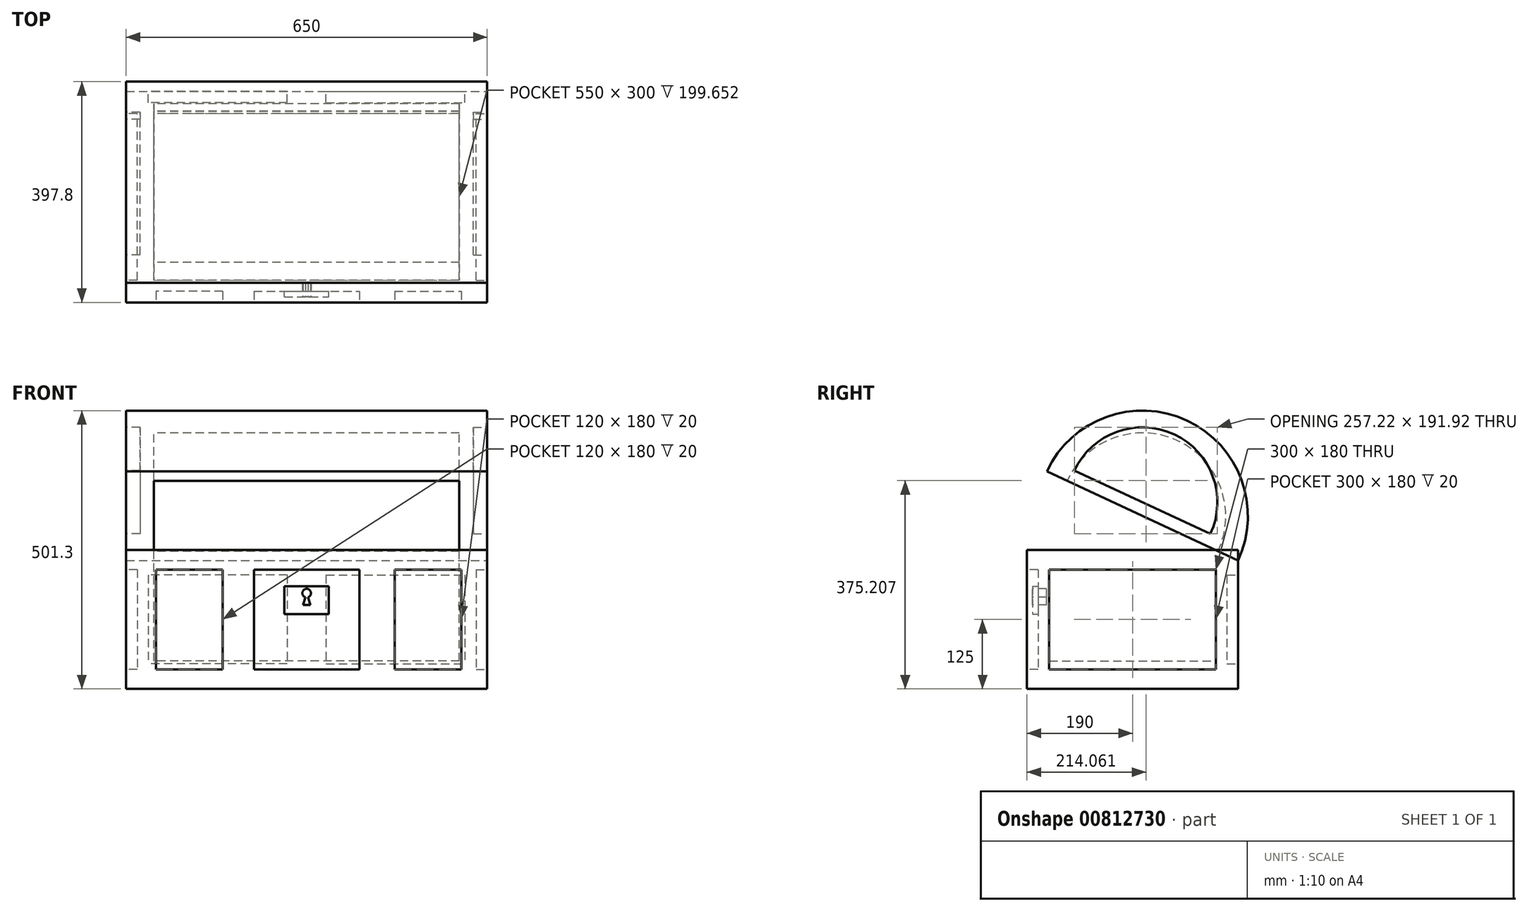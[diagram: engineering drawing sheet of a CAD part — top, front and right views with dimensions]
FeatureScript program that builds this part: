
annotation { "Feature Type Name" : "Feature", "Feature Type Description" : "" }
export const myFeature = defineFeature(function(context is Context, id is Id, definition is map)
    precondition{}
    {
        {
            var Q0;
            Q0=qCreatedBy(makeId("Top.planeOp"),FACE);
            var sketch = newSketch(context, id + "F0", { "sketchPlane" : qUnion([Q0])});
            skLineSegment(sketch, "E0.bottom", {"start": v(-32.5, 19) * mm, "end": v(32.5, 19) * mm});
            skLineSegment(sketch, "E0.top", {"start": v(-32.5, -19) * mm, "end": v(32.5, -19) * mm});
            skLineSegment(sketch, "E0.left", {"start": v(-32.5, 19) * mm, "end": v(-32.5, -19) * mm});
            skLineSegment(sketch, "E0.right", {"start": v(32.5, 19) * mm, "end": v(32.5, -19) * mm});
            skPoint(sketch, "E0.middle", {"position": v(0, 0) * mm});
            skSolve(sketch);
        }
        {
            var Q0;
            Q0 = qSketchRegion(id + "F0", true);
            extrude(context, id + "F1", {"entities" : qUnion([Q0]), "depth" : 25 * mm, "offsetDistance" : 25 * mm});
        }
        {
            var Q0;
            Q0=qCreatedBy(makeId("Right.planeOp"),FACE);
            var sketch = newSketch(context, id + "F2", { "sketchPlane" : qUnion([Q0])});
            skArc(sketch, "E1", {"start": v(-19, 23.1) * mm, "mid": v(-9.8, 48.35) * mm, "end": v(15.44, 39.16) * mm});
            skLineSegment(sketch, "E2", {"start": v(15.44, 39.16) * mm, "end": v(-19, 23.1) * mm});
            skSolve(sketch);
        }
        {
            var Q0;
            Q0 = qSketchRegion(id + "F2", true);
            extrude(context, id + "F3", {"entities" : qUnion([Q0]), "endBound" : BoundingType.SYMMETRIC, "depth" : 65 * mm, "offsetDistance" : 25 * mm});
        }
        {
            var Q0;
            Q0=qCreatedBy(makeId("Right.planeOp"),FACE);
            var sketch = newSketch(context, id + "F4", { "sketchPlane" : qUnion([Q0])});
            skArc(sketch, "E3", {"start": v(-15.37, 24.8) * mm, "mid": v(-8.12, 44.72) * mm, "end": v(11.81, 37.47) * mm});
            skLineSegment(sketch, "E4", {"start": v(11.81, 37.47) * mm, "end": v(-15.37, 24.8) * mm});
            skSolve(sketch);
        }
        {
            var Q0;
            Q0 = qSketchRegion(id + "F4", true);
            extrude(context, id + "F5", {"entities" : qUnion([Q0]), "operationType" : NewBodyOperationType.REMOVE, "endBound" : BoundingType.SYMMETRIC, "oppositeDirection" : true, "depth" : 55 * mm, "offsetDistance" : 25 * mm});
        }
        {
            var Q0;
            Q0=makeQuery(id+"F3.opExtrude","CAP_FACE",FACE,{"disambiguationData":[OSD([sQuery(id+"F2.wireOp",EDGE,"E1"),sQuery(id+"F2.wireOp",EDGE,"E2")])],"isStart":false});
            var sketch = newSketch(context, id + "F6", { "sketchPlane" : qUnion([Q0])});
            skArc(sketch, "E5", {"start": v(-14.02, 25.42) * mm, "mid": v(-7.49, 43.36) * mm, "end": v(10.46, 36.84) * mm});
            skLineSegment(sketch, "E6", {"start": v(-14.02, 25.42) * mm, "end": v(10.46, 36.84) * mm});
            skSolve(sketch);
        }
        {
            var Q0;
            Q0 = qSketchRegion(id + "F6", true);
            extrude(context, id + "F7", {"entities" : qUnion([Q0]), "oppositeDirection" : true, "depth" : 2.5 * mm, "offsetDistance" : 25 * mm});
        }
        {
            var Q0;
            Q0=makeQuery(id+"F7.opExtrude","SWEPT_BODY",BODY,{"disambiguationData":[OSD([sQuery(id+"F6.wireOp",EDGE,"E5"),sQuery(id+"F6.wireOp",EDGE,"E6")])]});
            transform(context, id + "F8", {"entities" : qUnion([Q0]), "transformType" : TransformType.TRANSLATION_3D, "dx" : 0 * mm, "dy" : 0 * mm, "dz" : 2.5 * mm, "makeCopy" : false});
        }
        {
            var Q0;
            Q0=makeQuery(id+"F7.opExtrude","SWEPT_BODY",BODY,{"disambiguationData":[OSD([sQuery(id+"F6.wireOp",EDGE,"E5"),sQuery(id+"F6.wireOp",EDGE,"E6")])]});
            var Q1;
            Q1=qCreatedBy(makeId("Right.planeOp"),FACE);
            mirror(context, id + "F9", {"entities" : qUnion([Q0]), "mirrorPlane" : qUnion([Q1])});
        }
        {
            var Q0;
            Q0=makeQuery(id+"F9.opPattern","COPY",BODY,{"derivedFrom":makeQuery(id+"F7.opExtrude","SWEPT_BODY",BODY,{"disambiguationData":[OSD([sQuery(id+"F6.wireOp",EDGE,"E5"),sQuery(id+"F6.wireOp",EDGE,"E6")])]}),"instanceName":"1"});
            var Q1;
            Q1=makeQuery(id+"F7.opExtrude","SWEPT_BODY",BODY,{"disambiguationData":[OSD([sQuery(id+"F6.wireOp",EDGE,"E5"),sQuery(id+"F6.wireOp",EDGE,"E6")])]});
            var Q2;
            Q2=makeQuery(id+"F3.opExtrude","SWEPT_BODY",BODY,{"disambiguationData":[OSD([sQuery(id+"F2.wireOp",EDGE,"E1"),sQuery(id+"F2.wireOp",EDGE,"E2")])]});
            booleanBodies(context, id + "F10", {"operationType" : BooleanOperationType.SUBTRACTION, "tools" : qUnion([Q0, Q1]), "targets" : qUnion([Q2])});
        }
        {
            var Q0;
            Q0=makeQuery(id+"F1.opExtrude","CAP_FACE",FACE,{"disambiguationData":[OSD([sQuery(id+"F0.wireOp",EDGE,"E0.bottom"),sQuery(id+"F0.wireOp",EDGE,"E0.top"),sQuery(id+"F0.wireOp",EDGE,"E0.left"),sQuery(id+"F0.wireOp",EDGE,"E0.right")])],"isStart":false});
            var sketch = newSketch(context, id + "F11", { "sketchPlane" : qUnion([Q0])});
            skLineSegment(sketch, "E7.bottom", {"start": v(-27.5, 15) * mm, "end": v(27.5, 15) * mm});
            skLineSegment(sketch, "E7.top", {"start": v(-27.5, -15) * mm, "end": v(27.5, -15) * mm});
            skLineSegment(sketch, "E7.left", {"start": v(-27.5, 15) * mm, "end": v(-27.5, -15) * mm});
            skLineSegment(sketch, "E7.right", {"start": v(27.5, 15) * mm, "end": v(27.5, -15) * mm});
            skPoint(sketch, "E7.middle", {"position": v(0, 0) * mm});
            skSolve(sketch);
        }
        {
            var Q0;
            Q0 = qSketchRegion(id + "F11", true);
            extrude(context, id + "F12", {"entities" : qUnion([Q0]), "operationType" : NewBodyOperationType.REMOVE, "oppositeDirection" : true, "depth" : 20 * mm, "offsetDistance" : 25 * mm});
        }
        {
            var Q0;
            Q0=makeQuery(id+"F1.opExtrude","SWEPT_FACE",FACE,{"disambiguationData":[OSD([sQuery(id+"F0.wireOp",EDGE,"E0.left")])]});
            var sketch = newSketch(context, id + "F13", { "sketchPlane" : qUnion([Q0])});
            skPoint(sketch, "E8", {"position": v(0, 12.5) * mm});
            skPoint(sketch, "E8.positionSnap0", {"position": v(-19, 12.5) * mm});
            skPoint(sketch, "E8.positionSnap1", {"position": v(0, 25) * mm});
            skLineSegment(sketch, "E9.bottom", {"start": v(-15, 21.5) * mm, "end": v(15, 21.5) * mm});
            skLineSegment(sketch, "E9.top", {"start": v(-15, 3.5) * mm, "end": v(15, 3.5) * mm});
            skLineSegment(sketch, "E9.left", {"start": v(-15, 21.5) * mm, "end": v(-15, 3.5) * mm});
            skLineSegment(sketch, "E9.right", {"start": v(15, 21.5) * mm, "end": v(15, 3.5) * mm});
            skSolve(sketch);
        }
        {
            var Q0;
            Q0 = qSketchRegion(id + "F13", true);
            extrude(context, id + "F14", {"entities" : qUnion([Q0]), "oppositeDirection" : true, "depth" : 2 * mm, "offsetDistance" : 25 * mm});
        }
        {
            var Q0;
            Q0=makeQuery(id+"F14.opExtrude","SWEPT_BODY",BODY,{"disambiguationData":[OSD([sQuery(id+"F13.wireOp",EDGE,"E9.bottom"),sQuery(id+"F13.wireOp",EDGE,"E9.top"),sQuery(id+"F13.wireOp",EDGE,"E9.left"),sQuery(id+"F13.wireOp",EDGE,"E9.right")])]});
            var Q1;
            Q1=qCreatedBy(makeId("Right.planeOp"),FACE);
            mirror(context, id + "F15", {"entities" : qUnion([Q0]), "mirrorPlane" : qUnion([Q1])});
        }
        {
            var Q0;
            Q0=makeQuery(id+"F15.opPattern","COPY",BODY,{"derivedFrom":makeQuery(id+"F14.opExtrude","SWEPT_BODY",BODY,{"disambiguationData":[OSD([sQuery(id+"F13.wireOp",EDGE,"E9.bottom"),sQuery(id+"F13.wireOp",EDGE,"E9.top"),sQuery(id+"F13.wireOp",EDGE,"E9.left"),sQuery(id+"F13.wireOp",EDGE,"E9.right")])]}),"instanceName":"1"});
            var Q1;
            Q1=makeQuery(id+"F14.opExtrude","SWEPT_BODY",BODY,{"disambiguationData":[OSD([sQuery(id+"F13.wireOp",EDGE,"E9.bottom"),sQuery(id+"F13.wireOp",EDGE,"E9.top"),sQuery(id+"F13.wireOp",EDGE,"E9.left"),sQuery(id+"F13.wireOp",EDGE,"E9.right")])]});
            var Q2;
            Q2=makeQuery(id+"F1.opExtrude","SWEPT_BODY",BODY,{"disambiguationData":[OSD([sQuery(id+"F0.wireOp",EDGE,"E0.bottom"),sQuery(id+"F0.wireOp",EDGE,"E0.top"),sQuery(id+"F0.wireOp",EDGE,"E0.left"),sQuery(id+"F0.wireOp",EDGE,"E0.right")])]});
            booleanBodies(context, id + "F16", {"operationType" : BooleanOperationType.SUBTRACTION, "tools" : qUnion([Q0, Q1]), "targets" : qUnion([Q2])});
        }
        {
            var Q0;
            Q0=makeQuery(id+"F1.opExtrude","SWEPT_FACE",FACE,{"disambiguationData":[OSD([sQuery(id+"F0.wireOp",EDGE,"E0.bottom")])]});
            var sketch = newSketch(context, id + "F17", { "sketchPlane" : qUnion([Q0])});
            skLineSegment(sketch, "E10.bottom", {"start": v(-9.5, 21.5) * mm, "end": v(9.5, 21.5) * mm});
            skLineSegment(sketch, "E10.top", {"start": v(-9.5, 3.5) * mm, "end": v(9.5, 3.5) * mm});
            skLineSegment(sketch, "E10.left", {"start": v(-9.5, 21.5) * mm, "end": v(-9.5, 3.5) * mm});
            skLineSegment(sketch, "E10.right", {"start": v(9.5, 21.5) * mm, "end": v(9.5, 3.5) * mm});
            skPoint(sketch, "E10.middle", {"position": v(0, 12.5) * mm});
            skPoint(sketch, "E10.middle.positionSnap0", {"position": v(-32.5, 12.5) * mm});
            skPoint(sketch, "E10.middle.positionSnap1", {"position": v(0, 25) * mm});
            skPoint(sketch, "E10.centerSnap0", {"position": v(-32.5, 12.5) * mm});
            skPoint(sketch, "E10.centerSnap1", {"position": v(0, 25) * mm});
            skLineSegment(sketch, "E11.bottom", {"start": v(-15.1, 21.5) * mm, "end": v(-27.1, 21.5) * mm});
            skLineSegment(sketch, "E11.top", {"start": v(-15.1, 3.5) * mm, "end": v(-27.1, 3.5) * mm});
            skLineSegment(sketch, "E11.left", {"start": v(-15.1, 21.5) * mm, "end": v(-15.1, 3.5) * mm});
            skLineSegment(sketch, "E11.right", {"start": v(-27.1, 21.5) * mm, "end": v(-27.1, 3.5) * mm});
            skPoint(sketch, "E11.middle", {"position": v(-21.1, 12.5) * mm});
            skLineSegment(sketch, "E12.bottom", {"start": v(15.85, 21.5) * mm, "end": v(27.85, 21.5) * mm});
            skLineSegment(sketch, "E12.top", {"start": v(15.85, 3.5) * mm, "end": v(27.85, 3.5) * mm});
            skLineSegment(sketch, "E12.left", {"start": v(15.85, 21.5) * mm, "end": v(15.85, 3.5) * mm});
            skLineSegment(sketch, "E12.right", {"start": v(27.85, 21.5) * mm, "end": v(27.85, 3.5) * mm});
            skPoint(sketch, "E12.middle", {"position": v(21.85, 12.5) * mm});
            skPoint(sketch, "E12.middle.positionSnap0", {"position": v(32.5, 12.5) * mm});
            skPoint(sketch, "E12.cornerSnap0", {"position": v(-21.1, 21.5) * mm});
            skPoint(sketch, "E12.centerSnap0", {"position": v(32.5, 12.5) * mm});
            skSolve(sketch);
        }
        {
            var Q0;
            Q0=makeQuery(id+"F17.imprint","IMPRINT",FACE,{"disambiguationData":[TD([[makeQuery(id+"F17.imprint","IMPRINT",EDGE,{"derivedFrom":sQuery(id+"F17.wireOp",EDGE,"E11.bottom")}),1.0]])]});
            var Q1;
            Q1=makeQuery(id+"F17.imprint","IMPRINT",FACE,{"disambiguationData":[TD([[makeQuery(id+"F17.imprint","IMPRINT",EDGE,{"derivedFrom":sQuery(id+"F17.wireOp",EDGE,"E10.bottom")}),-1.0]])]});
            var Q2;
            Q2=makeQuery(id+"F17.imprint","IMPRINT",FACE,{"disambiguationData":[TD([[makeQuery(id+"F17.imprint","IMPRINT",EDGE,{"derivedFrom":sQuery(id+"F17.wireOp",EDGE,"E12.bottom")}),-1.0]])]});
            extrude(context, id + "F18", {"entities" : qUnion([Q0, Q1, Q2]), "operationType" : NewBodyOperationType.REMOVE, "oppositeDirection" : true, "depth" : 2 * mm, "offsetDistance" : 25 * mm});
        }
        {
            var Q0;
            Q0=makeQuery(id+"F1.opExtrude","SWEPT_FACE",FACE,{"disambiguationData":[OSD([sQuery(id+"F0.wireOp",EDGE,"E0.top")])]});
            var sketch = newSketch(context, id + "F19", { "sketchPlane" : qUnion([Q0])});
            skLineSegment(sketch, "E13.bottom", {"start": v(-3.5, 20.5) * mm, "end": v(-28.5, 20.5) * mm});
            skLineSegment(sketch, "E13.top", {"start": v(-3.5, 4.5) * mm, "end": v(-28.5, 4.5) * mm});
            skLineSegment(sketch, "E13.left", {"start": v(-3.5, 20.5) * mm, "end": v(-3.5, 4.5) * mm});
            skLineSegment(sketch, "E13.right", {"start": v(-28.5, 20.5) * mm, "end": v(-28.5, 4.5) * mm});
            skPoint(sketch, "E13.middle", {"position": v(-16, 12.5) * mm});
            skPoint(sketch, "E13.middle.positionSnap0", {"position": v(-32.5, 12.5) * mm});
            skPoint(sketch, "E13.centerSnap0", {"position": v(-32.5, 12.5) * mm});
            skLineSegment(sketch, "E14.bottom", {"start": v(3.5, 20.5) * mm, "end": v(28.5, 20.5) * mm});
            skLineSegment(sketch, "E14.top", {"start": v(3.5, 4.5) * mm, "end": v(28.5, 4.5) * mm});
            skLineSegment(sketch, "E14.left", {"start": v(3.5, 20.5) * mm, "end": v(3.5, 4.5) * mm});
            skLineSegment(sketch, "E14.right", {"start": v(28.5, 20.5) * mm, "end": v(28.5, 4.5) * mm});
            skPoint(sketch, "E14.middle", {"position": v(16, 12.5) * mm});
            skSolve(sketch);
        }
        {
            var Q0;
            Q0=makeQuery(id+"F19.imprint","IMPRINT",FACE,{"disambiguationData":[TD([[makeQuery(id+"F19.imprint","IMPRINT",EDGE,{"derivedFrom":sQuery(id+"F19.wireOp",EDGE,"E13.bottom")}),1.0]])]});
            var Q1;
            Q1=makeQuery(id+"F19.imprint","IMPRINT",FACE,{"disambiguationData":[TD([[makeQuery(id+"F19.imprint","IMPRINT",EDGE,{"derivedFrom":sQuery(id+"F19.wireOp",EDGE,"E14.bottom")}),-1.0]])]});
            extrude(context, id + "F20", {"entities" : qUnion([Q0, Q1]), "operationType" : NewBodyOperationType.REMOVE, "oppositeDirection" : true, "depth" : 2 * mm, "offsetDistance" : 25 * mm});
        }
        {
            var Q0;
            Q0=makeQuery(id+"F18.boolean.opBoolean","COPY",FACE,{"derivedFrom":makeQuery(id+"F18.opExtrude","CAP_FACE",FACE,{"disambiguationData":[OSD([sQuery(id+"F17.wireOp",EDGE,"E10.bottom"),sQuery(id+"F17.wireOp",EDGE,"E10.top"),sQuery(id+"F17.wireOp",EDGE,"E10.left"),sQuery(id+"F17.wireOp",EDGE,"E10.right")])],"isStart":false})});
            var sketch = newSketch(context, id + "F21", { "sketchPlane" : qUnion([Q0])});
            skLineSegment(sketch, "E15.bottom", {"start": v(-4, 18.47) * mm, "end": v(4, 18.47) * mm});
            skLineSegment(sketch, "E15.top", {"start": v(-4, 13.47) * mm, "end": v(4, 13.47) * mm});
            skLineSegment(sketch, "E15.left", {"start": v(-4, 18.47) * mm, "end": v(-4, 13.47) * mm});
            skLineSegment(sketch, "E15.right", {"start": v(4, 18.47) * mm, "end": v(4, 13.47) * mm});
            skPoint(sketch, "E15.middle", {"position": v(0, 15.97) * mm});
            skSolve(sketch);
        }
        {
            var Q0;
            Q0 = qSketchRegion(id + "F21", true);
            extrude(context, id + "F22", {"entities" : qUnion([Q0]), "operationType" : NewBodyOperationType.ADD, "depth" : 1 * mm, "offsetDistance" : 25 * mm});
        }
        {
            var Q0;
            Q0=makeQuery(id+"F22.opExtrude","CAP_FACE",FACE,{"disambiguationData":[OSD([sQuery(id+"F21.wireOp",EDGE,"E15.bottom"),sQuery(id+"F21.wireOp",EDGE,"E15.top"),sQuery(id+"F21.wireOp",EDGE,"E15.left"),sQuery(id+"F21.wireOp",EDGE,"E15.right")])],"isStart":false});
            var sketch = newSketch(context, id + "F23", { "sketchPlane" : qUnion([Q0])});
            skCircle(sketch, "E16", {"center": v(0, 17.24) * mm, "radius": 0.78 * mm});
            skLineSegment(sketch, "E17", {"start": v(0, 15.12) * mm, "end": v(-0.65, 15.12) * mm});
            skLineSegment(sketch, "E18", {"start": v(-0.65, 15.12) * mm, "end": v(0, 17.24) * mm});
            skLineSegment(sketch, "E19.MirrorCS", {"start": v(0.65, 15.12) * mm, "end": v(0, 17.24) * mm});
            skLineSegment(sketch, "E20.MirrorCS", {"start": v(0, 15.12) * mm, "end": v(0.65, 15.12) * mm});
            skSolve(sketch);
        }
        {
            var Q0;
            Q0 = qSketchRegion(id + "F23", true);
            extrude(context, id + "F24", {"entities" : qUnion([Q0]), "operationType" : NewBodyOperationType.REMOVE, "oppositeDirection" : true, "depth" : 2.5 * mm, "offsetDistance" : 25 * mm});
        }
        {
            var Q0;
            Q0=makeQuery(id+"F1.opExtrude","SWEPT_BODY",BODY,{"disambiguationData":[OSD([sQuery(id+"F0.wireOp",EDGE,"E0.bottom"),sQuery(id+"F0.wireOp",EDGE,"E0.top"),sQuery(id+"F0.wireOp",EDGE,"E0.left"),sQuery(id+"F0.wireOp",EDGE,"E0.right")])]});
            var Q1;
            Q1=makeQuery(id+"F3.opExtrude","SWEPT_BODY",BODY,{"disambiguationData":[OSD([sQuery(id+"F2.wireOp",EDGE,"E1"),sQuery(id+"F2.wireOp",EDGE,"E2")])]});
            var Q2;
            Q2=makeQuery(id+"F1.opExtrude","SWEPT_EDGE",EDGE,{"disambiguationData":[OSD([sQuery(id+"F0.wireOp",EDGE,"E0.top"),sQuery(id+"F0.wireOp",EDGE,"E0.right")])]});
            transform(context, id + "F25", {"entities" : qUnion([Q0, Q1]), "transformType" : TransformType.ROTATION, "transformAxis" : qUnion([Q2]), "angle" : 180 * degree, "makeCopy" : false});
        }
        {
            var Q0;
            Q0=makeQuery(id+"F3.opExtrude","SWEPT_BODY",BODY,{"disambiguationData":[OSD([sQuery(id+"F2.wireOp",EDGE,"E1"),sQuery(id+"F2.wireOp",EDGE,"E2")])]});
            var Q1;
            Q1=makeQuery(id+"F1.opExtrude","SWEPT_BODY",BODY,{"disambiguationData":[OSD([sQuery(id+"F0.wireOp",EDGE,"E0.bottom"),sQuery(id+"F0.wireOp",EDGE,"E0.top"),sQuery(id+"F0.wireOp",EDGE,"E0.left"),sQuery(id+"F0.wireOp",EDGE,"E0.right")])]});
            transform(context, id + "F26", {"entities" : qUnion([Q0, Q1]), "transformType" : TransformType.TRANSLATION_3D, "dx" : -65 * mm, "dy" : 38 * mm, "dz" : 0 * mm, "makeCopy" : false});
        }
        {
            var Q0;
            Q0=makeQuery(id+"F3.opExtrude","SWEPT_BODY",BODY,{"disambiguationData":[OSD([sQuery(id+"F2.wireOp",EDGE,"E1"),sQuery(id+"F2.wireOp",EDGE,"E2")])]});
            var Q1;
            Q1=makeQuery(id+"F1.opExtrude","SWEPT_BODY",BODY,{"disambiguationData":[OSD([sQuery(id+"F0.wireOp",EDGE,"E0.bottom"),sQuery(id+"F0.wireOp",EDGE,"E0.top"),sQuery(id+"F0.wireOp",EDGE,"E0.left"),sQuery(id+"F0.wireOp",EDGE,"E0.right")])]});
            var Q2;
            Q2=qCreatedBy(makeId("Origin.pointOp"),VERTEX);
            transform(context, id + "F27", {"entities" : qUnion([Q0, Q1]), "transformType" : TransformType.SCALE_UNIFORMLY, "scale" : 10, "scalePoint" : qUnion([Q2]), "makeCopy" : false});
        }
    });
